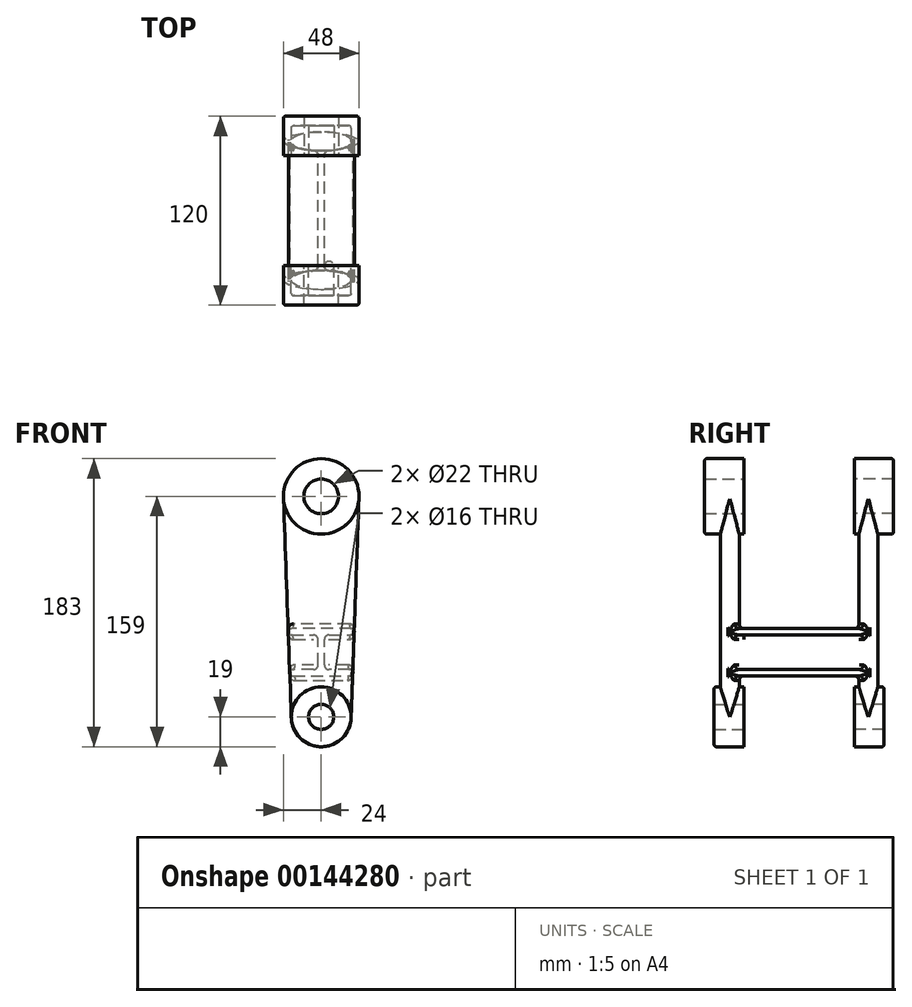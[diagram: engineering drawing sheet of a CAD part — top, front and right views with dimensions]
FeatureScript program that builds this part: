
annotation { "Feature Type Name" : "Feature", "Feature Type Description" : "" }
export const myFeature = defineFeature(function(context is Context, id is Id, definition is map)
    precondition{}
    {
        {
            var Q0;
            Q0=qCreatedBy(makeId("Front.planeOp"),FACE);
            var sketch = newSketch(context, id + "F0", { "sketchPlane" : qUnion([Q0])});
            skCircle(sketch, "E0", {"center": v(0, 0) * mm, "radius": 8 * mm});
            skCircle(sketch, "E1", {"center": v(0, 0) * mm, "radius": 19 * mm});
            skCircle(sketch, "E2", {"center": v(0, 140) * mm, "radius": 11 * mm});
            skCircle(sketch, "E3", {"center": v(0, 140) * mm, "radius": 24 * mm});
            skSolve(sketch);
        }
        {
            var Q0;
            Q0=makeQuery(id+"F0.imprint","IMPRINT",FACE,{"disambiguationData":[TD([[makeQuery(id+"F0.imprint","IMPRINT",EDGE,{"derivedFrom":sQuery(id+"F0.wireOp",EDGE,"E2")}),-1.0]])]});
            extrude(context, id + "F1", {"entities" : qUnion([Q0]), "depth" : 25 * mm});
        }
        {
            var Q0;
            Q0=makeQuery(id+"F0.imprint","IMPRINT",FACE,{"disambiguationData":[TD([[makeQuery(id+"F0.imprint","IMPRINT",EDGE,{"derivedFrom":sQuery(id+"F0.wireOp",EDGE,"E0")}),-1.0]])]});
            extrude(context, id + "F2", {"entities" : qUnion([Q0]), "depth" : 19 * mm});
        }
        {
            var Q0;
            Q0=qCreatedBy(makeId("Top.planeOp"),FACE);
            var sketch = newSketch(context, id + "F3", { "sketchPlane" : qUnion([Q0])});
            skEllipse(sketch, "E4", {"center": v(0, -9) * mm, "majorRadius": 19 * mm, "minorRadius": 6 * mm, "majorAxis": v(1, 0)});
            skPoint(sketch, "E5", {"position": v(0, -3) * mm});
            skLineSegment(sketch, "E6", {"start": v(19, 0) * mm, "end": v(19, -19) * mm, "construction": true});
            skSolve(sketch);
        }
        {
            var Q0;
            Q0=sQuery(id+"F0.wireOp",VERTEX,"E3.center");
            var Q1;
            Q1=qCreatedBy(makeId("Top.planeOp"),FACE);
            cPlane(context, id + "F4", {"entities" : qUnion([Q0, Q1]), "cplaneType" : CPlaneType.PLANE_POINT, "offset" : 25 * mm, "width" : 150 * mm, "height" : 150 * mm});
        }
        {
            var Q0;
            Q0=qCreatedBy(id+"F4.planeOp",FACE);
            var sketch = newSketch(context, id + "F5", { "sketchPlane" : qUnion([Q0])});
            skEllipse(sketch, "E7", {"center": v(0, -9) * mm, "majorRadius": 24 * mm, "minorRadius": 6 * mm, "majorAxis": v(1, 0)});
            skPoint(sketch, "E8", {"position": v(0, -3) * mm});
            skLineSegment(sketch, "E9", {"start": v(24, 0) * mm, "end": v(24, -25) * mm, "construction": true});
            skSolve(sketch);
        }
        {
            var Q0;
            Q0=makeQuery(id+"F5.imprint","IMPRINT",FACE,{"disambiguationData":[TD([[makeQuery(id+"F5.imprint","IMPRINT",EDGE,{"derivedFrom":sQuery(id+"F5.wireOp",EDGE,"E7")}),1.0]])]});
            var Q1;
            Q1=makeQuery(id+"F3.imprint","IMPRINT",FACE,{"disambiguationData":[TD([[makeQuery(id+"F3.imprint","IMPRINT",EDGE,{"derivedFrom":sQuery(id+"F3.wireOp",EDGE,"E4")}),1.0]])]});
            loft(context, id + "F6", {"operationType" : NewBodyOperationType.ADD, "sheetProfilesArray" : [{ "sheetProfileEntities" : qUnion([Q0]) }, { "sheetProfileEntities" : qUnion([Q1]) }]});
        }
        {
            var Q0;
            Q0=makeQuery(id+"F0.imprint","IMPRINT",FACE,{"disambiguationData":[TD([[makeQuery(id+"F0.imprint","IMPRINT",EDGE,{"derivedFrom":sQuery(id+"F0.wireOp",EDGE,"E2")}),1.0]])]});
            var Q1;
            Q1=makeQuery(id+"F0.imprint","IMPRINT",FACE,{"disambiguationData":[TD([[makeQuery(id+"F0.imprint","IMPRINT",EDGE,{"derivedFrom":sQuery(id+"F0.wireOp",EDGE,"E0")}),1.0]])]});
            extrude(context, id + "F7", {"entities" : qUnion([Q0, Q1]), "operationType" : NewBodyOperationType.REMOVE, "endBound" : BoundingType.THROUGH_ALL, "depth" : 25 * mm});
        }
        {
            var Q0;
            Q0=makeQuery(id+"F0.imprint","IMPRINT",FACE,{"disambiguationData":[TD([[makeQuery(id+"F0.imprint","IMPRINT",EDGE,{"derivedFrom":sQuery(id+"F0.wireOp",EDGE,"E0")}),-1.0]])]});
            var sketch = newSketch(context, id + "F8", { "sketchPlane" : qUnion([Q0])});
            skLineSegment(sketch, "E10", {"start": v(0, 0) * mm, "end": v(0, 26) * mm, "construction": true});
            skLineSegment(sketch, "E11", {"start": v(22.6, 26) * mm, "end": v(-23.07, 26) * mm});
            skLineSegment(sketch, "E12", {"start": v(19, 56) * mm, "end": v(-18.86, 56) * mm});
            skLineSegment(sketch, "E13", {"start": v(19, 52) * mm, "end": v(2, 52) * mm});
            skLineSegment(sketch, "E14", {"start": v(22.6, 30) * mm, "end": v(2, 30) * mm});
            skLineSegment(sketch, "E15", {"start": v(0, 26) * mm, "end": v(0, 56) * mm, "construction": true});
            skPoint(sketch, "E15.endSnap0", {"position": v(-0.23, 56) * mm});
            skLineSegment(sketch, "E16", {"start": v(-2, 52) * mm, "end": v(-2, 30) * mm});
            skLineSegment(sketch, "E17", {"start": v(2, 52) * mm, "end": v(2, 30) * mm});
            skLineSegment(sketch, "E18.trimOffspring", {"start": v(-2, 52) * mm, "end": v(-18.86, 52) * mm});
            skLineSegment(sketch, "E19.trimOffspring", {"start": v(-2, 30) * mm, "end": v(-22.67, 30) * mm});
            skLineSegment(sketch, "E20", {"start": v(19, 54) * mm, "end": v(14.38, 54) * mm, "construction": true});
            skArc(sketch, "E21", {"start": v(19, 56) * mm, "mid": v(21, 54) * mm, "end": v(19, 52) * mm});
            skArc(sketch, "E22", {"start": v(-18.86, 56) * mm, "mid": v(-20.86, 54) * mm, "end": v(-18.86, 52) * mm});
            skPoint(sketch, "E23.orphan", {"position": v(-24.24, 56) * mm});
            skPoint(sketch, "E24.orphan", {"position": v(23.78, 56) * mm});
            skLineSegment(sketch, "E25", {"start": v(18.12, 28) * mm, "end": v(-17.82, 28) * mm, "construction": true});
            skArc(sketch, "E26", {"start": v(18.12, 30) * mm, "mid": v(20.12, 28) * mm, "end": v(18.12, 26) * mm});
            skArc(sketch, "E27", {"start": v(-17.82, 30) * mm, "mid": v(-19.82, 28) * mm, "end": v(-17.82, 26) * mm});
            skSolve(sketch);
        }
        {
            var Q0;
            Q0=makeQuery(id+"F0.imprint","IMPRINT",FACE,{"disambiguationData":[TD([[makeQuery(id+"F0.imprint","IMPRINT",EDGE,{"derivedFrom":sQuery(id+"F0.wireOp",EDGE,"E2")}),-1.0]])]});
            cPlane(context, id + "F9", {"entities" : qUnion([Q0]), "cplaneType" : CPlaneType.OFFSET, "offset" : 35 * mm, "oppositeDirection" : true, "width" : 150 * mm, "height" : 150 * mm});
        }
        {
            var Q0;
            Q0=makeQuery(id+"F1.opExtrude","SWEPT_BODY",BODY,{"disambiguationData":[OSD([sQuery(id+"F0.wireOp",EDGE,"E2"),sQuery(id+"F0.wireOp",EDGE,"E3")])]});
            var Q1;
            Q1=qCreatedBy(id+"F9.planeOp",FACE);
            mirror(context, id + "F10", {"entities" : qUnion([Q0]), "mirrorPlane" : qUnion([Q1])});
        }
        {
            var Q0;
            Q0=makeQuery(id+"F8.imprint","IMPRINT",FACE,{"disambiguationData":[TD([[makeQuery(id+"F8.imprint","IMPRINT",EDGE,{"derivedFrom":sQuery(id+"F8.wireOp",EDGE,"E12")}),1.0]])]});
            var Q1;
            Q1=makeQuery(id+"F6.boolean.opBoolean","SPLIT",FACE,{"disambiguationData":[TD([makeQuery(id+"F1.opExtrude","SWEPT_FACE",FACE,{"disambiguationData":[OSD([sQuery(id+"F0.wireOp",EDGE,"E3")])]}),makeQuery(id+"F2.opExtrude","SWEPT_FACE",FACE,{"disambiguationData":[OSD([sQuery(id+"F0.wireOp",EDGE,"E1")])]})])],"derivedFrom":makeQuery(id+"F6.opLoft","SWEPT_FACE",FACE,{"disambiguationData":[OSD([sQuery(id+"F3.wireOp",EDGE,"E4"),sQuery(id+"F5.wireOp",EDGE,"E7")])]})});
            var Q2;
            Q2=makeQuery(id+"F10.opPattern","COPY",FACE,{"derivedFrom":makeQuery(id+"F6.boolean.opBoolean","SPLIT",FACE,{"disambiguationData":[TD([makeQuery(id+"F1.opExtrude","SWEPT_FACE",FACE,{"disambiguationData":[OSD([sQuery(id+"F0.wireOp",EDGE,"E3")])]}),makeQuery(id+"F2.opExtrude","SWEPT_FACE",FACE,{"disambiguationData":[OSD([sQuery(id+"F0.wireOp",EDGE,"E1")])]})])],"derivedFrom":makeQuery(id+"F6.opLoft","SWEPT_FACE",FACE,{"disambiguationData":[OSD([sQuery(id+"F3.wireOp",EDGE,"E4"),sQuery(id+"F5.wireOp",EDGE,"E7")])]})}),"instanceName":"1"});
            extrude(context, id + "F11", {"entities" : qUnion([Q0]), "operationType" : NewBodyOperationType.ADD, "endBoundEntityFace" : qUnion([Q1]), "depth" : 10 * mm, "hasSecondDirection" : true, "secondDirectionOppositeDirection" : true, "secondDirectionBoundEntityFace" : qUnion([Q2]), "secondDirectionDepth" : 80 * mm});
        }
        {
            var Q0;
            Q0=makeQuery(id+"F11.opExtrude","SWEPT_EDGE",EDGE,{"disambiguationData":[OSD([sQuery(id+"F8.wireOp",EDGE,"E14"),sQuery(id+"F8.wireOp",EDGE,"E17")])]});
            var Q1;
            Q1=makeQuery(id+"F11.opExtrude","SWEPT_EDGE",EDGE,{"disambiguationData":[OSD([sQuery(id+"F8.wireOp",EDGE,"E13"),sQuery(id+"F8.wireOp",EDGE,"E17")])]});
            var Q2;
            Q2=makeQuery(id+"F11.boolean.opBoolean","INTERSECT",EDGE,{"derivedFrom":[makeQuery(id+"F6.boolean.opBoolean","SPLIT",FACE,{"disambiguationData":[TD([makeQuery(id+"F1.opExtrude","SWEPT_FACE",FACE,{"disambiguationData":[OSD([sQuery(id+"F0.wireOp",EDGE,"E3")])]}),makeQuery(id+"F2.opExtrude","SWEPT_FACE",FACE,{"disambiguationData":[OSD([sQuery(id+"F0.wireOp",EDGE,"E1")])]})])],"derivedFrom":makeQuery(id+"F6.opLoft","SWEPT_FACE",FACE,{"disambiguationData":[OSD([sQuery(id+"F3.wireOp",EDGE,"E4"),sQuery(id+"F5.wireOp",EDGE,"E7")])]})}),makeQuery(id+"F11.opExtrude","SWEPT_FACE",FACE,{"disambiguationData":[OSD([sQuery(id+"F8.wireOp",EDGE,"E17")])]})]});
            var Q3;
            Q3=makeQuery(id+"F11.opExtrude","SWEPT_FACE",FACE,{"disambiguationData":[OSD([sQuery(id+"F8.wireOp",EDGE,"E13")])]});
            var Q4;
            Q4=makeQuery(id+"F11.opExtrude","SWEPT_FACE",FACE,{"disambiguationData":[OSD([sQuery(id+"F8.wireOp",EDGE,"E14")])]});
            var Q5;
            Q5=makeQuery(id+"F11.boolean.opBoolean","INTERSECT",EDGE,{"derivedFrom":[makeQuery(id+"F10.opPattern","COPY",FACE,{"derivedFrom":makeQuery(id+"F6.boolean.opBoolean","SPLIT",FACE,{"disambiguationData":[TD([makeQuery(id+"F1.opExtrude","SWEPT_FACE",FACE,{"disambiguationData":[OSD([sQuery(id+"F0.wireOp",EDGE,"E3")])]}),makeQuery(id+"F2.opExtrude","SWEPT_FACE",FACE,{"disambiguationData":[OSD([sQuery(id+"F0.wireOp",EDGE,"E1")])]})])],"derivedFrom":makeQuery(id+"F6.opLoft","SWEPT_FACE",FACE,{"disambiguationData":[OSD([sQuery(id+"F3.wireOp",EDGE,"E4"),sQuery(id+"F5.wireOp",EDGE,"E7")])]})}),"instanceName":"1"}),makeQuery(id+"F11.opExtrude","SWEPT_FACE",FACE,{"disambiguationData":[OSD([sQuery(id+"F8.wireOp",EDGE,"E17")])]})]});
            fillet(context, id + "F12", {"entities" : qUnion([Q0, Q1, Q2, Q3, Q4, Q5]), "radius" : 3 * mm, "tangentPropagation" : true, "allowEdgeOverflow" : false});
        }
        {
            var Q0;
            Q0=makeQuery(id+"F11.boolean.opBoolean","INTERSECT",EDGE,{"derivedFrom":[makeQuery(id+"F6.boolean.opBoolean","SPLIT",FACE,{"disambiguationData":[TD([makeQuery(id+"F1.opExtrude","SWEPT_FACE",FACE,{"disambiguationData":[OSD([sQuery(id+"F0.wireOp",EDGE,"E3")])]}),makeQuery(id+"F2.opExtrude","SWEPT_FACE",FACE,{"disambiguationData":[OSD([sQuery(id+"F0.wireOp",EDGE,"E1")])]})])],"derivedFrom":makeQuery(id+"F6.opLoft","SWEPT_FACE",FACE,{"disambiguationData":[OSD([sQuery(id+"F3.wireOp",EDGE,"E4"),sQuery(id+"F5.wireOp",EDGE,"E7")])]})}),makeQuery(id+"F11.opExtrude","SWEPT_FACE",FACE,{"disambiguationData":[OSD([sQuery(id+"F8.wireOp",EDGE,"E16")])]})]});
            var Q1;
            Q1=makeQuery(id+"F11.opExtrude","SWEPT_EDGE",EDGE,{"disambiguationData":[OSD([sQuery(id+"F8.wireOp",EDGE,"E16"),sQuery(id+"F8.wireOp",EDGE,"E19.trimOffspring")])]});
            var Q2;
            Q2=makeQuery(id+"F11.boolean.opBoolean","INTERSECT",EDGE,{"derivedFrom":[makeQuery(id+"F6.boolean.opBoolean","SPLIT",FACE,{"disambiguationData":[TD([makeQuery(id+"F1.opExtrude","SWEPT_FACE",FACE,{"disambiguationData":[OSD([sQuery(id+"F0.wireOp",EDGE,"E3")])]}),makeQuery(id+"F2.opExtrude","SWEPT_FACE",FACE,{"disambiguationData":[OSD([sQuery(id+"F0.wireOp",EDGE,"E1")])]})])],"derivedFrom":makeQuery(id+"F6.opLoft","SWEPT_FACE",FACE,{"disambiguationData":[OSD([sQuery(id+"F3.wireOp",EDGE,"E4"),sQuery(id+"F5.wireOp",EDGE,"E7")])]})}),makeQuery(id+"F11.opExtrude","SWEPT_FACE",FACE,{"disambiguationData":[OSD([sQuery(id+"F8.wireOp",EDGE,"E19.trimOffspring")])]})]});
            var Q3;
            Q3=makeQuery(id+"F11.boolean.opBoolean","INTERSECT",EDGE,{"derivedFrom":[makeQuery(id+"F6.boolean.opBoolean","SPLIT",FACE,{"disambiguationData":[TD([makeQuery(id+"F1.opExtrude","SWEPT_FACE",FACE,{"disambiguationData":[OSD([sQuery(id+"F0.wireOp",EDGE,"E3")])]}),makeQuery(id+"F2.opExtrude","SWEPT_FACE",FACE,{"disambiguationData":[OSD([sQuery(id+"F0.wireOp",EDGE,"E1")])]})])],"derivedFrom":makeQuery(id+"F6.opLoft","SWEPT_FACE",FACE,{"disambiguationData":[OSD([sQuery(id+"F3.wireOp",EDGE,"E4"),sQuery(id+"F5.wireOp",EDGE,"E7")])]})}),makeQuery(id+"F11.opExtrude","SWEPT_FACE",FACE,{"disambiguationData":[OSD([sQuery(id+"F8.wireOp",EDGE,"E18.trimOffspring")])]})]});
            var Q4;
            Q4=makeQuery(id+"F11.boolean.opBoolean","INTERSECT",EDGE,{"derivedFrom":[makeQuery(id+"F10.opPattern","COPY",FACE,{"derivedFrom":makeQuery(id+"F6.boolean.opBoolean","SPLIT",FACE,{"disambiguationData":[TD([makeQuery(id+"F1.opExtrude","SWEPT_FACE",FACE,{"disambiguationData":[OSD([sQuery(id+"F0.wireOp",EDGE,"E3")])]}),makeQuery(id+"F2.opExtrude","SWEPT_FACE",FACE,{"disambiguationData":[OSD([sQuery(id+"F0.wireOp",EDGE,"E1")])]})])],"derivedFrom":makeQuery(id+"F6.opLoft","SWEPT_FACE",FACE,{"disambiguationData":[OSD([sQuery(id+"F3.wireOp",EDGE,"E4"),sQuery(id+"F5.wireOp",EDGE,"E7")])]})}),"instanceName":"1"}),makeQuery(id+"F11.opExtrude","SWEPT_FACE",FACE,{"disambiguationData":[OSD([sQuery(id+"F8.wireOp",EDGE,"E16")])]})]});
            var Q5;
            Q5=makeQuery(id+"F11.opExtrude","SWEPT_EDGE",EDGE,{"disambiguationData":[OSD([sQuery(id+"F8.wireOp",EDGE,"E16"),sQuery(id+"F8.wireOp",EDGE,"E18.trimOffspring")])]});
            var Q6;
            Q6=makeQuery(id+"F11.boolean.opBoolean","INTERSECT",EDGE,{"derivedFrom":[makeQuery(id+"F10.opPattern","COPY",FACE,{"derivedFrom":makeQuery(id+"F6.boolean.opBoolean","SPLIT",FACE,{"disambiguationData":[TD([makeQuery(id+"F1.opExtrude","SWEPT_FACE",FACE,{"disambiguationData":[OSD([sQuery(id+"F0.wireOp",EDGE,"E3")])]}),makeQuery(id+"F2.opExtrude","SWEPT_FACE",FACE,{"disambiguationData":[OSD([sQuery(id+"F0.wireOp",EDGE,"E1")])]})])],"derivedFrom":makeQuery(id+"F6.opLoft","SWEPT_FACE",FACE,{"disambiguationData":[OSD([sQuery(id+"F3.wireOp",EDGE,"E4"),sQuery(id+"F5.wireOp",EDGE,"E7")])]})}),"instanceName":"1"}),makeQuery(id+"F11.opExtrude","SWEPT_FACE",FACE,{"disambiguationData":[OSD([sQuery(id+"F8.wireOp",EDGE,"E18.trimOffspring")])]})]});
            var Q7;
            Q7=makeQuery(id+"F11.boolean.opBoolean","INTERSECT",EDGE,{"derivedFrom":[makeQuery(id+"F10.opPattern","COPY",FACE,{"derivedFrom":makeQuery(id+"F6.boolean.opBoolean","SPLIT",FACE,{"disambiguationData":[TD([makeQuery(id+"F1.opExtrude","SWEPT_FACE",FACE,{"disambiguationData":[OSD([sQuery(id+"F0.wireOp",EDGE,"E3")])]}),makeQuery(id+"F2.opExtrude","SWEPT_FACE",FACE,{"disambiguationData":[OSD([sQuery(id+"F0.wireOp",EDGE,"E1")])]})])],"derivedFrom":makeQuery(id+"F6.opLoft","SWEPT_FACE",FACE,{"disambiguationData":[OSD([sQuery(id+"F3.wireOp",EDGE,"E4"),sQuery(id+"F5.wireOp",EDGE,"E7")])]})}),"instanceName":"1"}),makeQuery(id+"F11.opExtrude","SWEPT_FACE",FACE,{"disambiguationData":[OSD([sQuery(id+"F8.wireOp",EDGE,"E19.trimOffspring")])]})]});
            fillet(context, id + "F13", {"entities" : qUnion([Q0, Q1, Q2, Q3, Q4, Q5, Q6, Q7]), "radius" : 3 * mm, "tangentPropagation" : true, "allowEdgeOverflow" : false});
        }
        {
            var Q0;
            Q0=makeQuery(id+"F1.opExtrude","CAP_EDGE",EDGE,{"disambiguationData":[OSD([sQuery(id+"F0.wireOp",EDGE,"E3")])],"isStart":false});
            var Q1;
            Q1=makeQuery(id+"F10.opPattern","COPY",EDGE,{"derivedFrom":makeQuery(id+"F1.opExtrude","CAP_EDGE",EDGE,{"disambiguationData":[OSD([sQuery(id+"F0.wireOp",EDGE,"E3")])],"isStart":false}),"instanceName":"1"});
            var Q2;
            Q2=makeQuery(id+"F10.opPattern","COPY",EDGE,{"derivedFrom":makeQuery(id+"F2.opExtrude","CAP_EDGE",EDGE,{"disambiguationData":[OSD([sQuery(id+"F0.wireOp",EDGE,"E1")])],"isStart":false}),"instanceName":"1"});
            var Q3;
            Q3=makeQuery(id+"F2.opExtrude","CAP_EDGE",EDGE,{"disambiguationData":[OSD([sQuery(id+"F0.wireOp",EDGE,"E1")])],"isStart":false});
            fillet(context, id + "F14", {"entities" : qUnion([Q0, Q1, Q2, Q3]), "radius" : 1.5 * mm, "tangentPropagation" : true, "allowEdgeOverflow" : false});
        }
    });
